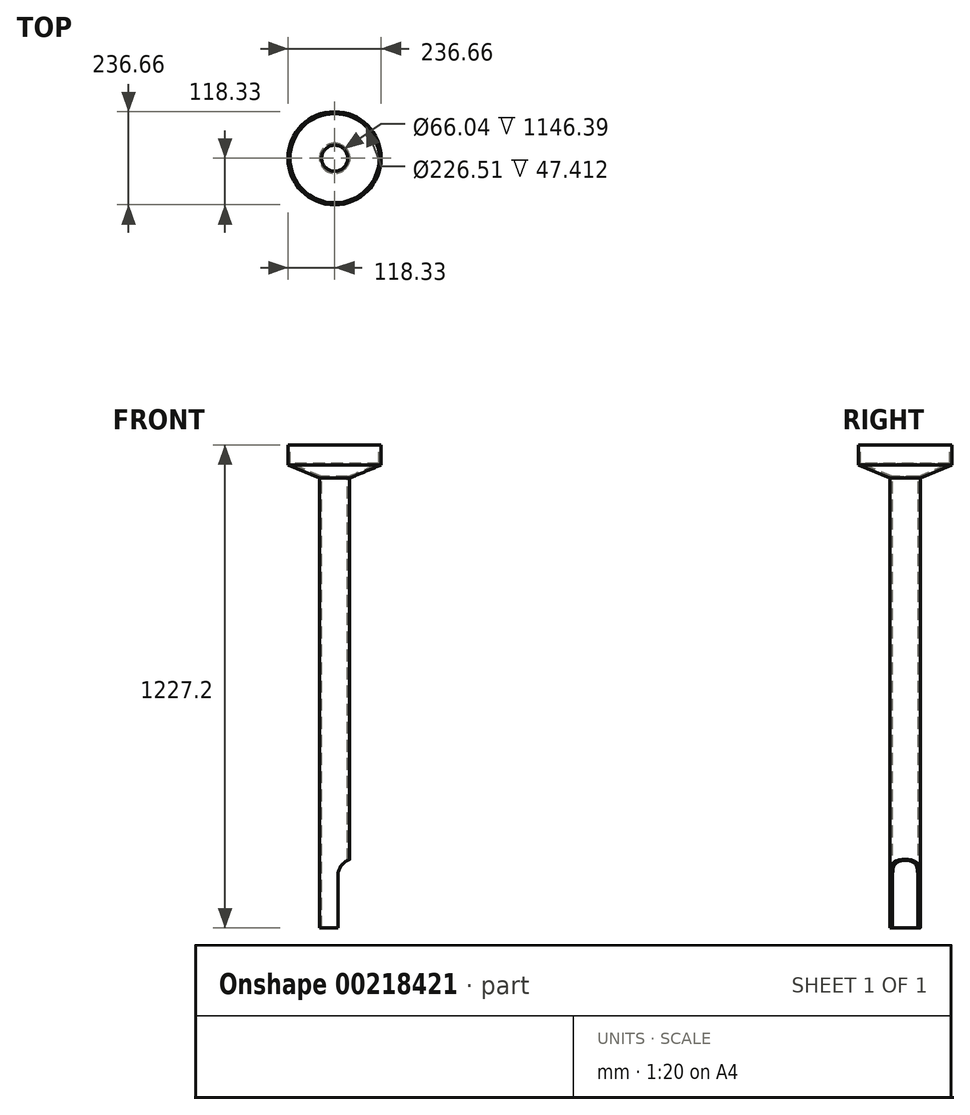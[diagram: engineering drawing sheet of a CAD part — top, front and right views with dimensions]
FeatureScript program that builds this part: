
annotation { "Feature Type Name" : "Feature", "Feature Type Description" : "" }
export const myFeature = defineFeature(function(context is Context, id is Id, definition is map)
    precondition{}
    {
        {
            var Q0;
            Q0=qCreatedBy(makeId("Front.planeOp"),FACE);
            var sketch = newSketch(context, id + "F0", { "sketchPlane" : qUnion([Q0])});
            skLineSegment(sketch, "E0", {"start": v(0, 84.2) * mm, "end": v(0, -1143) * mm, "construction": true});
            skLineSegment(sketch, "E1", {"start": v(-113.25, 84.2) * mm, "end": v(-118.33, 84.2) * mm});
            skLineSegment(sketch, "E2", {"start": v(-118.33, 84.2) * mm, "end": v(-118.33, 33.4) * mm});
            skLineSegment(sketch, "E3", {"start": v(-118.33, 33.4) * mm, "end": v(-38.1, 0) * mm});
            skLineSegment(sketch, "E4", {"start": v(-38.1, 0) * mm, "end": v(-38.1, -1143) * mm});
            skLineSegment(sketch, "E5", {"start": v(-38.1, -1143) * mm, "end": v(-33.02, -1143) * mm});
            skLineSegment(sketch, "E6.1", {"start": v(-113.25, 84.2) * mm, "end": v(-113.25, 36.8) * mm});
            skLineSegment(sketch, "E6.2", {"start": v(-113.25, 36.8) * mm, "end": v(-33.02, 3.39) * mm});
            skLineSegment(sketch, "E6.4", {"start": v(-33.02, 3.39) * mm, "end": v(-33.02, -1143) * mm});
            skSolve(sketch);
        }
        {
            var Q0;
            {var subQ1=sQuery(id+"F0.wireOp",EDGE,"E2");Q0=makeQuery(id+"F0.imprint","IMPRINT",FACE,{"disambiguationData":[TD([[makeQuery(id+"F0.imprint","IMPRINT",EDGE,{"derivedFrom":subQ1}),1.0]])]});}
            var Q1;
            Q1=sQuery(id+"F0.wireOp",EDGE,"E0");
            revolve(context, id + "F1", {"entities" : qUnion([Q0]), "axis" : qUnion([Q1]), "revolveType" : RevolveType.FULL});
        }
        {
            var Q0;
            Q0=qCreatedBy(makeId("Front.planeOp"),FACE);
            var sketch = newSketch(context, id + "F2", { "sketchPlane" : qUnion([Q0])});
            skLineSegment(sketch, "E7", {"start": v(8.06, -1153.51) * mm, "end": v(58.46, -1153.51) * mm});
            skLineSegment(sketch, "E8", {"start": v(8.06, -1153.51) * mm, "end": v(8.06, -1012.1) * mm});
            skLineSegment(sketch, "E9", {"start": v(58.46, -1153.51) * mm, "end": v(58.46, -966.39) * mm});
            skLineSegment(sketch, "E10", {"start": v(53.78, -966.39) * mm, "end": v(58.46, -966.39) * mm});
            skPoint(sketch, "E11.visualSharp", {"position": v(8.06, -966.39) * mm});
            skArc(sketch, "E11.filletArc", {"start": v(53.78, -966.39) * mm, "mid": v(21.45, -979.78) * mm, "end": v(8.06, -1012.1) * mm});
            skSolve(sketch);
        }
        {
            var Q0;
            {var subQ0=sQuery(id+"F2.wireOp",EDGE,"E7");Q0=makeQuery(id+"F2.imprint","IMPRINT",FACE,{"disambiguationData":[TD([[makeQuery(id+"F2.imprint","IMPRINT",EDGE,{"derivedFrom":subQ0}),1.0]])]});}
            extrude(context, id + "F3", {"entities" : qUnion([Q0]), "operationType" : NewBodyOperationType.REMOVE, "endBound" : BoundingType.SYMMETRIC, "oppositeDirection" : true, "depth" : 127 * mm});
        }
    });
